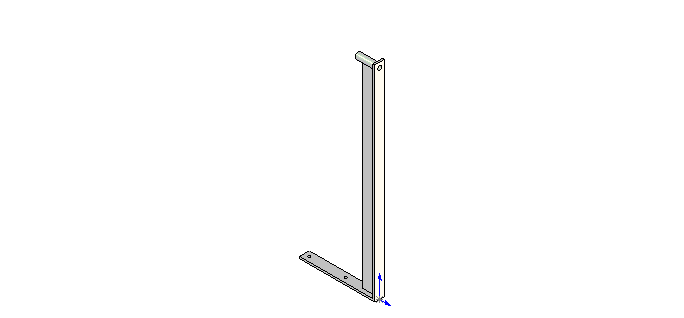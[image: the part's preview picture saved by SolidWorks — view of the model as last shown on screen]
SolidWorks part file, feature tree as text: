
SOLIDWORKS PART (.sldprt)
format: sldprt  version: not decoded by parser v0  size: 237,056 bytes
history: native  units: mm
features: sketch x5, plane x3, extrude x3, cut_extrude x2 + 1 further entry (+7 scaffold rows collapsed)
feature tree (21):
  scaffold x7  (default folders/planes/origin — collapsed)
  "Corps de surface"
  plane  "Face"
  plane  "Dessus"
  plane  "Droite"
  sketch  "Esquisse1"  dims[c1.D1=4.0mm c1.D2=4.0mm c1.D3=400.0mm c1.D4=150.0mm c2.D1=4.0mm c2.D2=4.0mm c2.D3=150.0mm c2.D4=420.0mm]
  extrude  "Extrusion4"  Depth=10mm
  sketch  "Esquisse2"  dims[c1.D1=60.0mm c1.D2=30.0mm c2.D1=400.0mm]
  extrude  "Extrusion5"  Depth=2mm
  sketch  "Esquisse3"  dims[c1.D1=5.0mm c1.D2=5.0mm c1.D5=5.0mm c1.D3=10.0mm c1.D4=75.0mm c2.D5=65.0mm c2.D6=4.0mm]
  cut_extrude  "Enlèv. mat.-Extru.1"  [1 undecoded]
  sketch  "Esquisse4"  dims[D2=8.0mm D1=10.0mm]
  cut_extrude  "Enlèv. mat.-Extru.2"  [1 undecoded]
  sketch  "Esquisse6"  dims[D1=12.5mm D2=8.0mm]
  extrude  "Extrusion8"  Depth=40mm
decode coverage: 8 of 10 modeling features carry decoded parameters; 1 rows unclassified (native names shown)
note: 2 parameter values undecoded
note: suppression state not decoded; provenance and decode notes live in map.json
